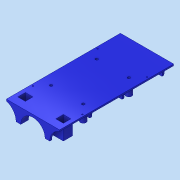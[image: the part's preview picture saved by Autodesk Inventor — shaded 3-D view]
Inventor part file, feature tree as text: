
AUTODESK INVENTOR PART (.ipt)
format: ipt  version: 2022 (Build 260153000, 153)  size: 260,608 bytes
history: native  units: in
note: dims shown in document units (in); Inventor stores cm internally (conversion verified against a paired STEP export)
features: projected_geometry x4, other x3, extrude x2, sketch x2
ambient origin geometry x8: Origin, YZ Plane, XZ Plane, XY Plane, X Axis, Y Axis, Z Axis, Center Point
bodies: Solid1 (feature_tree)
feature tree (11):
  other  "electronics.ipt"
  extrude  "Extrusion1"  Depth=0.3937in TaperAngle=0.0deg
  extrude  "Extrusion2"  Depth=1.122in TaperAngle=0.0deg
  other  "Solid4::electronics.ipt"
  other  "TaggingFeature1"
  sketch  "Sketch1"  dims[d0=0.3937in d1=1.0in d2=0.0in]
  projected_geometry  "Projected Loop1"
  projected_geometry  "Projected Loop2"
  projected_geometry  "Projected Loop3"
  projected_geometry  "Projected Loop4"
  sketch  "Sketch2"  dims[d3=0.2756in d4=1.122in d5=0.0in]
